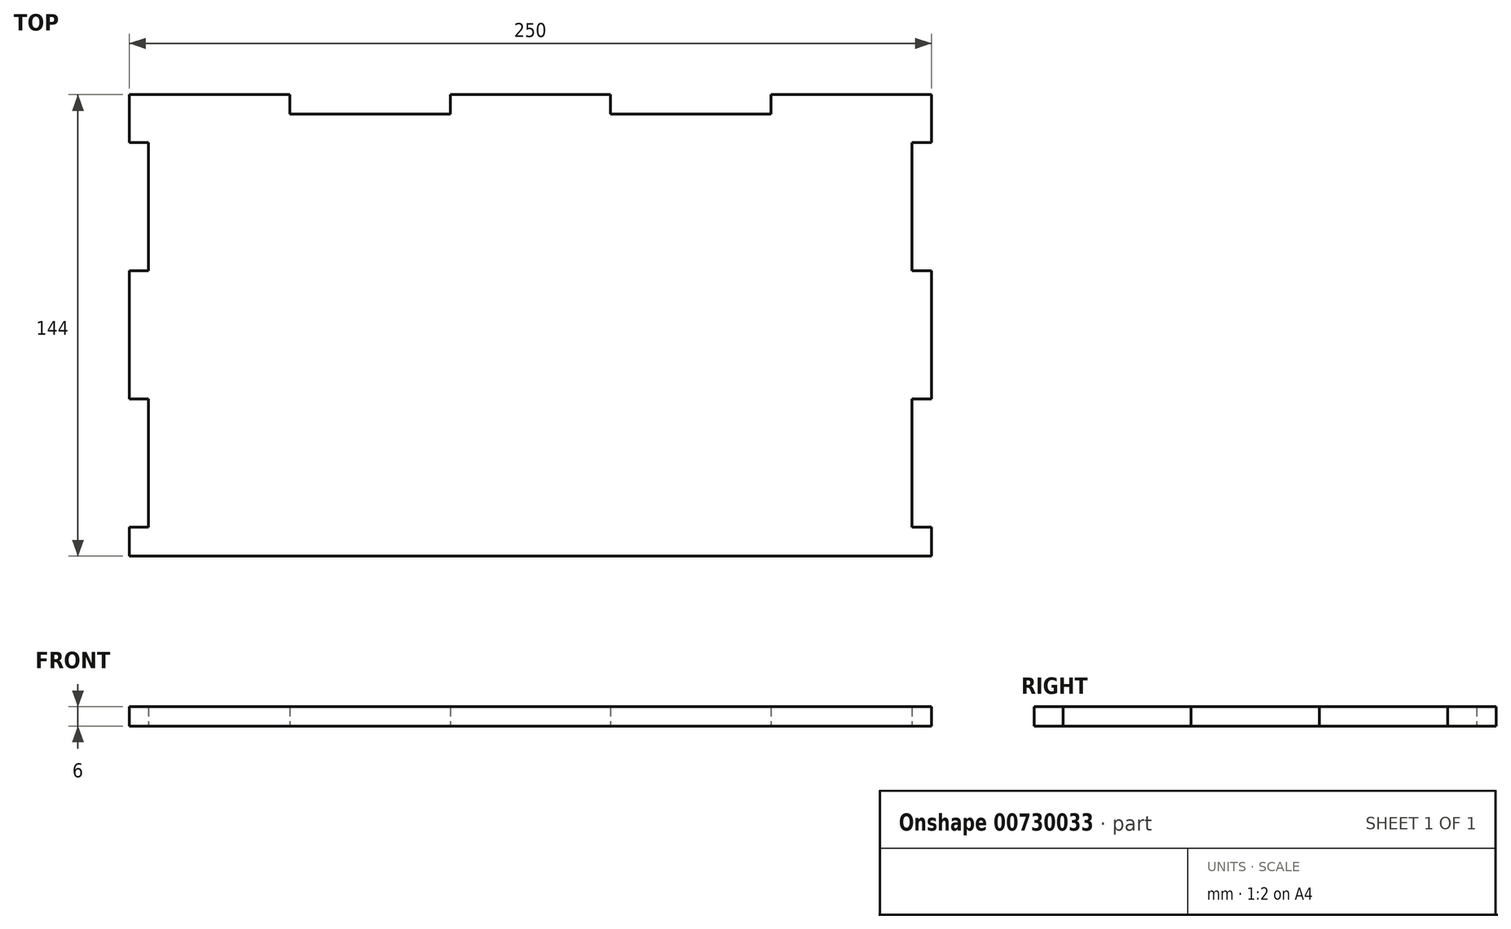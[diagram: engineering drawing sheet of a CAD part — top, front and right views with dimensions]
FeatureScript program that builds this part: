
annotation { "Feature Type Name" : "Feature", "Feature Type Description" : "" }
export const myFeature = defineFeature(function(context is Context, id is Id, definition is map)
    precondition{}
    {
        {
            var Q0;
            Q0=qCreatedBy(makeId("Top.planeOp"),FACE);
            var sketch = newSketch(context, id + "F0", { "sketchPlane" : qUnion([Q0])});
            skLineSegment(sketch, "E0", {"start": v(-64.48, -52.84) * mm, "end": v(-58.48, -52.84) * mm});
            skLineSegment(sketch, "E1", {"start": v(-58.48, -52.84) * mm, "end": v(-58.48, -12.84) * mm});
            skLineSegment(sketch, "E2", {"start": v(-58.48, -12.84) * mm, "end": v(-64.48, -12.84) * mm});
            skLineSegment(sketch, "E3", {"start": v(-64.48, -12.84) * mm, "end": v(-64.48, 27.16) * mm});
            skLineSegment(sketch, "E4", {"start": v(-64.48, 27.16) * mm, "end": v(-58.48, 27.16) * mm});
            skLineSegment(sketch, "E5", {"start": v(-58.48, 27.16) * mm, "end": v(-58.48, 67.16) * mm});
            skLineSegment(sketch, "E6", {"start": v(-58.48, 67.16) * mm, "end": v(-64.48, 67.16) * mm});
            skLineSegment(sketch, "E7", {"start": v(-64.48, 67.16) * mm, "end": v(-64.48, 82.16) * mm});
            skLineSegment(sketch, "E8", {"start": v(-64.48, 82.16) * mm, "end": v(-14.48, 82.16) * mm});
            skLineSegment(sketch, "E9", {"start": v(-14.48, 82.16) * mm, "end": v(-14.48, 76.16) * mm});
            skLineSegment(sketch, "E10", {"start": v(-14.48, 76.16) * mm, "end": v(35.52, 76.16) * mm});
            skLineSegment(sketch, "E11", {"start": v(35.52, 76.16) * mm, "end": v(35.52, 82.16) * mm});
            skLineSegment(sketch, "E12", {"start": v(35.52, 82.16) * mm, "end": v(85.52, 82.16) * mm});
            skLineSegment(sketch, "E13", {"start": v(85.52, 82.16) * mm, "end": v(85.52, 76.16) * mm});
            skLineSegment(sketch, "E14", {"start": v(85.52, 76.16) * mm, "end": v(135.52, 76.16) * mm});
            skLineSegment(sketch, "E15", {"start": v(135.52, 76.16) * mm, "end": v(135.52, 82.16) * mm});
            skLineSegment(sketch, "E16", {"start": v(135.52, 82.16) * mm, "end": v(185.52, 82.16) * mm});
            skLineSegment(sketch, "E17", {"start": v(185.52, 82.16) * mm, "end": v(185.52, 67.16) * mm});
            skLineSegment(sketch, "E18", {"start": v(185.52, 67.16) * mm, "end": v(179.52, 67.16) * mm});
            skLineSegment(sketch, "E19", {"start": v(179.52, 67.16) * mm, "end": v(179.52, 27.16) * mm});
            skLineSegment(sketch, "E20", {"start": v(179.52, 27.16) * mm, "end": v(185.52, 27.16) * mm});
            skLineSegment(sketch, "E21", {"start": v(185.52, 27.16) * mm, "end": v(185.52, -12.84) * mm});
            skLineSegment(sketch, "E22", {"start": v(185.52, -12.84) * mm, "end": v(179.52, -12.84) * mm});
            skLineSegment(sketch, "E23", {"start": v(179.52, -12.84) * mm, "end": v(179.52, -52.84) * mm});
            skLineSegment(sketch, "E24", {"start": v(179.52, -52.84) * mm, "end": v(185.52, -52.84) * mm});
            skLineSegment(sketch, "E25", {"start": v(-64.48, -52.84) * mm, "end": v(-64.48, -61.84) * mm});
            skLineSegment(sketch, "E26", {"start": v(185.52, -52.84) * mm, "end": v(185.52, -61.84) * mm});
            skLineSegment(sketch, "E27", {"start": v(-64.48, -61.84) * mm, "end": v(185.52, -61.84) * mm});
            skSolve(sketch);
        }
        {
            var Q0;
            Q0 = qSketchRegion(id + "F0", true);
            extrude(context, id + "F1", {"entities" : qUnion([Q0]), "depth" : 6 * mm, "offsetDistance" : 25 * mm});
        }
    });
